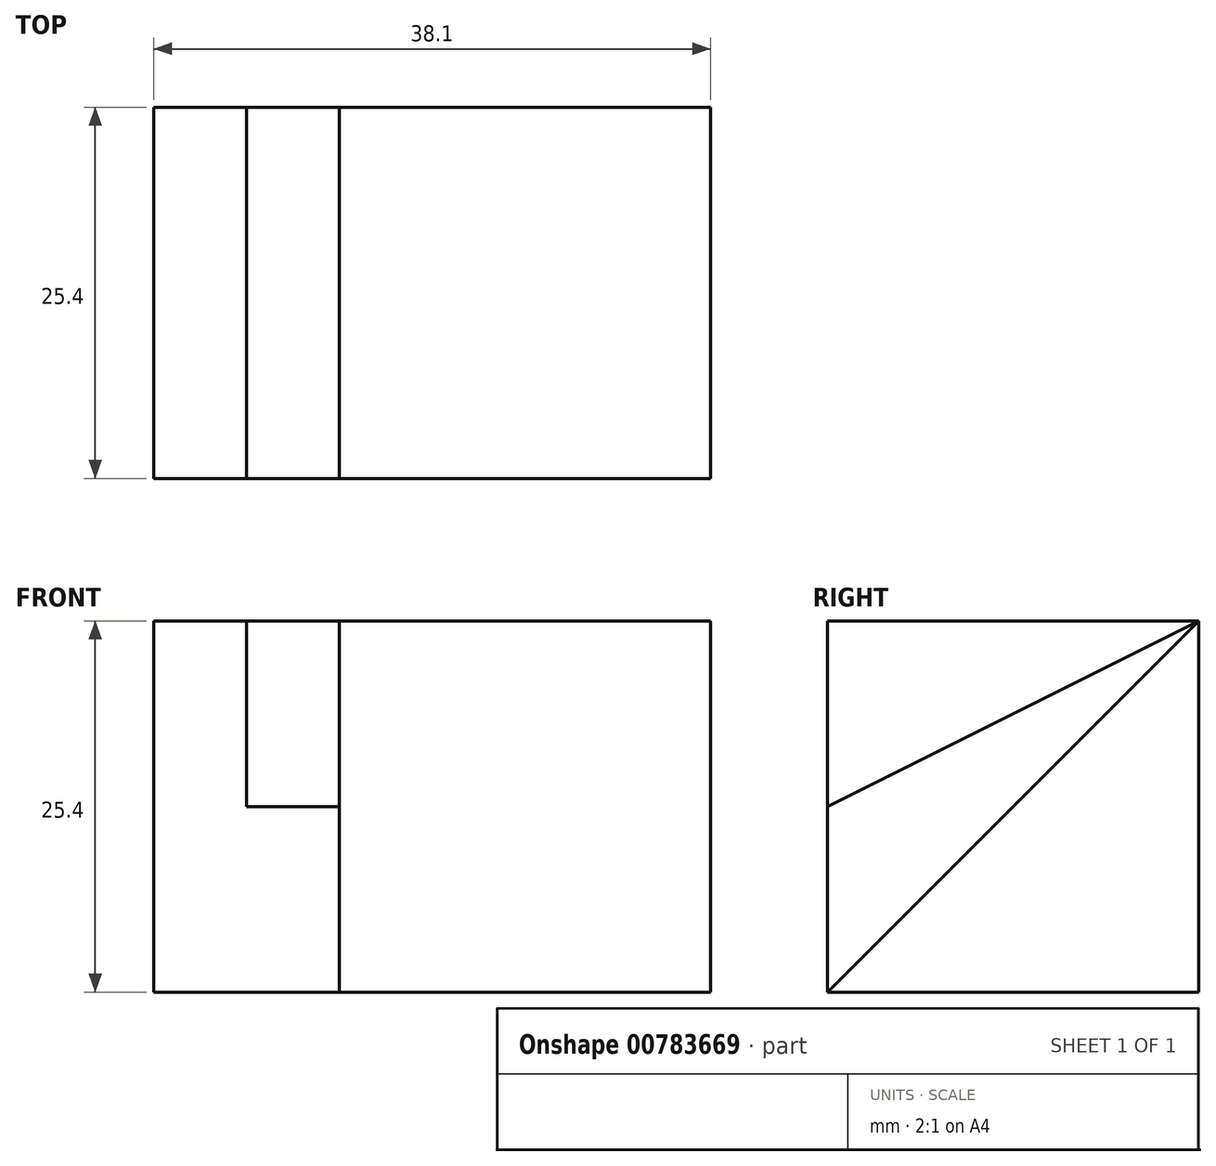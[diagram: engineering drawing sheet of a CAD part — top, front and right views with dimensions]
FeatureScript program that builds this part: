
annotation { "Feature Type Name" : "Feature", "Feature Type Description" : "" }
export const myFeature = defineFeature(function(context is Context, id is Id, definition is map)
    precondition{}
    {
        {
            var Q0;
            Q0=qCreatedBy(makeId("Front.planeOp"),FACE);
            var sketch = newSketch(context, id + "F0", { "sketchPlane" : qUnion([Q0])});
            skLineSegment(sketch, "E0", {"start": v(0, 0) * mm, "end": v(38.1, 0) * mm});
            skLineSegment(sketch, "E1", {"start": v(38.1, 0) * mm, "end": v(38.1, 25.4) * mm});
            skLineSegment(sketch, "E2", {"start": v(38.1, 25.4) * mm, "end": v(0, 25.4) * mm});
            skLineSegment(sketch, "E3", {"start": v(0, 25.4) * mm, "end": v(0, 0) * mm});
            skSolve(sketch);
        }
        {
            var Q0;
            Q0 = qSketchRegion(id + "F0", true);
            extrude(context, id + "F1", {"entities" : qUnion([Q0]), "depth" : 25.4 * mm, "offsetDistance" : 25.4 * mm});
        }
        {
            var Q0;
            Q0=makeQuery(id+"F1.opExtrude","SWEPT_FACE",FACE,{"disambiguationData":[OSD([sQuery(id+"F0.wireOp",EDGE,"E1")])]});
            var sketch = newSketch(context, id + "F2", { "sketchPlane" : qUnion([Q0])});
            skLineSegment(sketch, "E4", {"start": v(0, 25.4) * mm, "end": v(-25.4, 0) * mm});
            skLineSegment(sketch, "E5", {"start": v(-25.4, 0) * mm, "end": v(-25.4, 12.7) * mm});
            skLineSegment(sketch, "E6", {"start": v(-25.4, 12.7) * mm, "end": v(0, 25.4) * mm});
            skSolve(sketch);
        }
        {
            var Q0;
            {var subQ0=sQuery(id+"F2.wireOp",EDGE,"E6");Q0=makeQuery(id+"F2.imprint","IMPRINT",FACE,{"disambiguationData":[TD([[makeQuery(id+"F2.imprint","IMPRINT",EDGE,{"derivedFrom":subQ0}),1.0]])]});}
            extrude(context, id + "F3", {"entities" : qUnion([Q0]), "operationType" : NewBodyOperationType.REMOVE, "oppositeDirection" : true, "depth" : 31.75 * mm, "offsetDistance" : 25.4 * mm});
        }
        {
            var Q0;
            Q0=makeQuery(id+"F1.opExtrude","SWEPT_FACE",FACE,{"disambiguationData":[OSD([sQuery(id+"F0.wireOp",EDGE,"E1")])]});
            var sketch = newSketch(context, id + "F4", { "sketchPlane" : qUnion([Q0])});
            skLineSegment(sketch, "E7", {"start": v(-25.4, 0) * mm, "end": v(0, 25.4) * mm});
            skSolve(sketch);
        }
        {
            var Q0;
            Q0=makeQuery(id+"F4.imprint","IMPRINT",FACE,{"disambiguationData":[TD([[makeQuery(id+"F4.imprint","IMPRINT",EDGE,{"derivedFrom":sQuery(id+"F4.wireOp",EDGE,"E7")}),1.0]])]});
            extrude(context, id + "F5", {"entities" : qUnion([Q0]), "operationType" : NewBodyOperationType.REMOVE, "oppositeDirection" : true, "depth" : 25.4 * mm, "offsetDistance" : 25.4 * mm});
        }
    });
